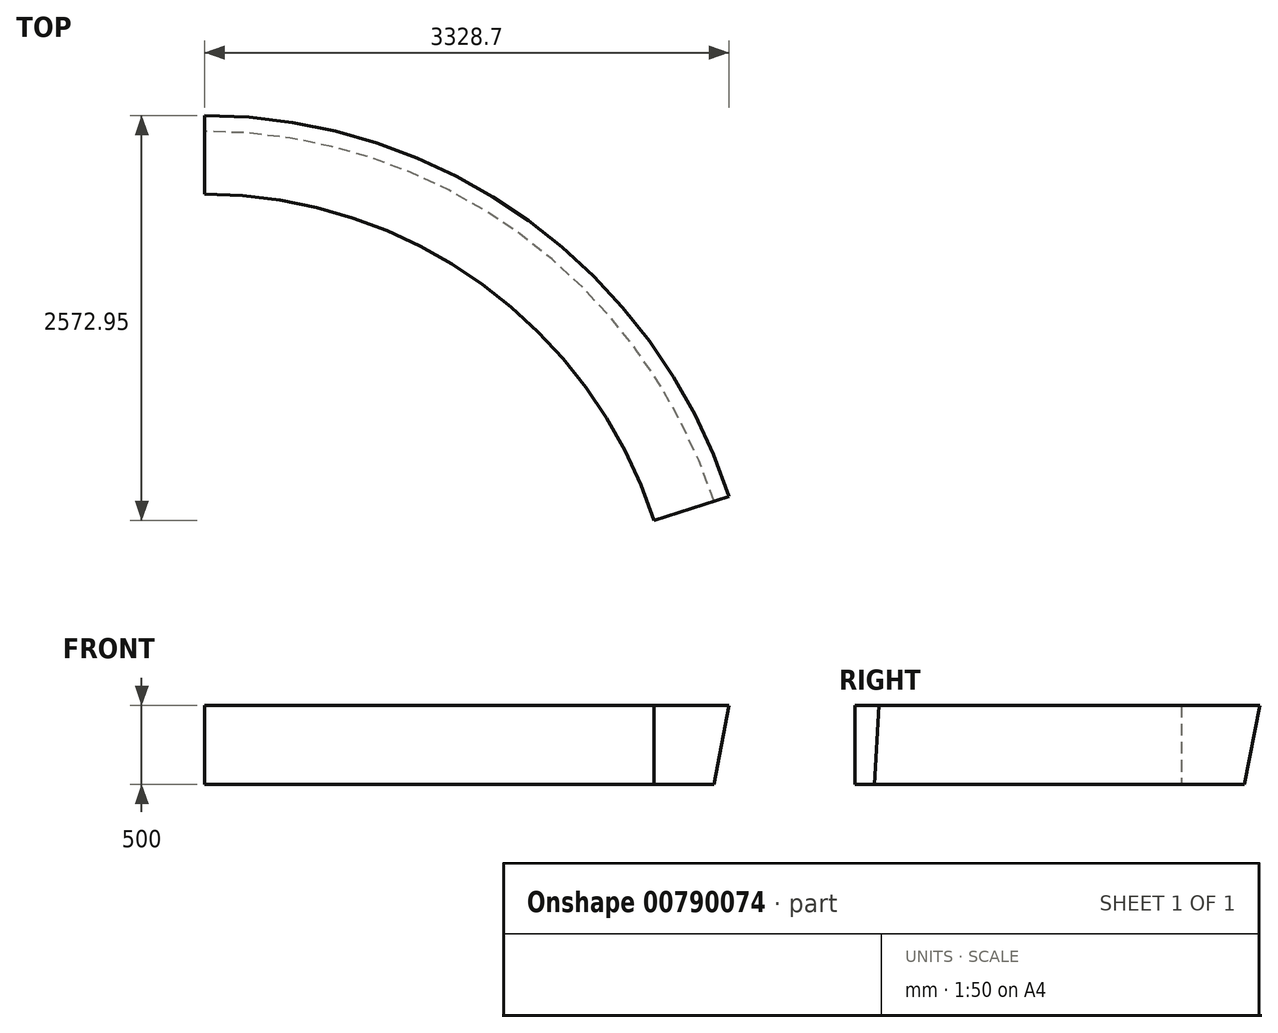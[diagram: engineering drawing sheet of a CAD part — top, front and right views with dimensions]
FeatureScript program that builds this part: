
annotation { "Feature Type Name" : "Feature", "Feature Type Description" : "" }
export const myFeature = defineFeature(function(context is Context, id is Id, definition is map)
    precondition{}
    {
        {
            var Q0;
            Q0=qCreatedBy(makeId("Right.planeOp"),FACE);
            var sketch = newSketch(context, id + "F0", { "sketchPlane" : qUnion([Q0])});
            skLineSegment(sketch, "E0", {"start": v(0, 0) * mm, "end": v(0, 500) * mm});
            skLineSegment(sketch, "E1", {"start": v(0, 500) * mm, "end": v(500, 500) * mm});
            skLineSegment(sketch, "E2", {"start": v(500, 500) * mm, "end": v(400, 0) * mm});
            skLineSegment(sketch, "E3", {"start": v(400, 0) * mm, "end": v(0, 0) * mm});
            skLineSegment(sketch, "E4", {"start": v(0, 0) * mm, "end": v(-3000, 0) * mm, "construction": true});
            skLineSegment(sketch, "E5", {"start": v(-3000, 0) * mm, "end": v(-3000, 500) * mm, "construction": true});
            skSolve(sketch);
        }
        {
            var Q0;
            Q0 = qSketchRegion(id + "F0", true);
            var Q1;
            Q1=sQuery(id+"F0.wireOp",EDGE,"E5");
            revolve(context, id + "F1", {"surfaceOperationType" : NewSurfaceOperationType.NEW, "entities" : qUnion([Q0]), "axis" : qUnion([Q1]), "revolveType" : RevolveType.FULL});
        }
        {
            var Q0;
            Q0=qCreatedBy(makeId("Top.planeOp"),FACE);
            var sketch = newSketch(context, id + "F2", { "sketchPlane" : qUnion([Q0])});
            skLineSegment(sketch, "E6", {"start": v(0, 0) * mm, "end": v(0, -3000) * mm});
            skLineSegment(sketch, "E7", {"start": v(0, 0) * mm, "end": v(0, 914.9) * mm});
            skLineSegment(sketch, "E8", {"start": v(0, -3000) * mm, "end": v(3723.29, -1790.23) * mm});
            skCircle(sketch, "E9", {"center": v(0, -3000) * mm, "radius": 3914.9 * mm});
            skSolve(sketch);
        }
        {
            var Q0;
            Q0=makeQuery(id+"F2.imprint","IMPRINT",FACE,{"disambiguationData":[TD([[makeQuery(id+"F2.imprint","IMPRINT",EDGE,{"derivedFrom":sQuery(id+"F2.wireOp",EDGE,"E6")}),-1.0]])]});
            extrude(context, id + "F3", {"entities" : qUnion([Q0]), "operationType" : NewBodyOperationType.REMOVE, "depth" : 2220 * mm, "offsetDistance" : 25 * mm});
        }
    });
